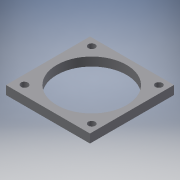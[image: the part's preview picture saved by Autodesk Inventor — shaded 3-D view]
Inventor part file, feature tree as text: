
AUTODESK INVENTOR PART (.ipt)
format: ipt  version: 2018 (Build 220112000, 112)  size: 180,224 bytes
history: native  units: mm
features: other x3, extrude x1, sketch x1, reference x1
ambient origin geometry x8: Origin, YZ Plane, XZ Plane, XY Plane, X Axis, Y Axis, Z Axis, Center Point
bodies: Solid1 (feature_tree)
feature tree (6):
  extrude  "Extrusion1"  Depth=4.0mm TaperAngle=0.0deg
  sketch  "Sketch1"  dims[d0=38.8mm d1=4.0mm d2=0.0mm d3=23.0mm]
  reference  "Reference1"
  other  "<userpath>\OneDrive\SL-Inventor\The Beast v1.2 PackandGo\Workspaces\Workspace\Assembly33.iam"
  other  "Assembly33.iam"
  other  "Z Motor Mount Right:1"
